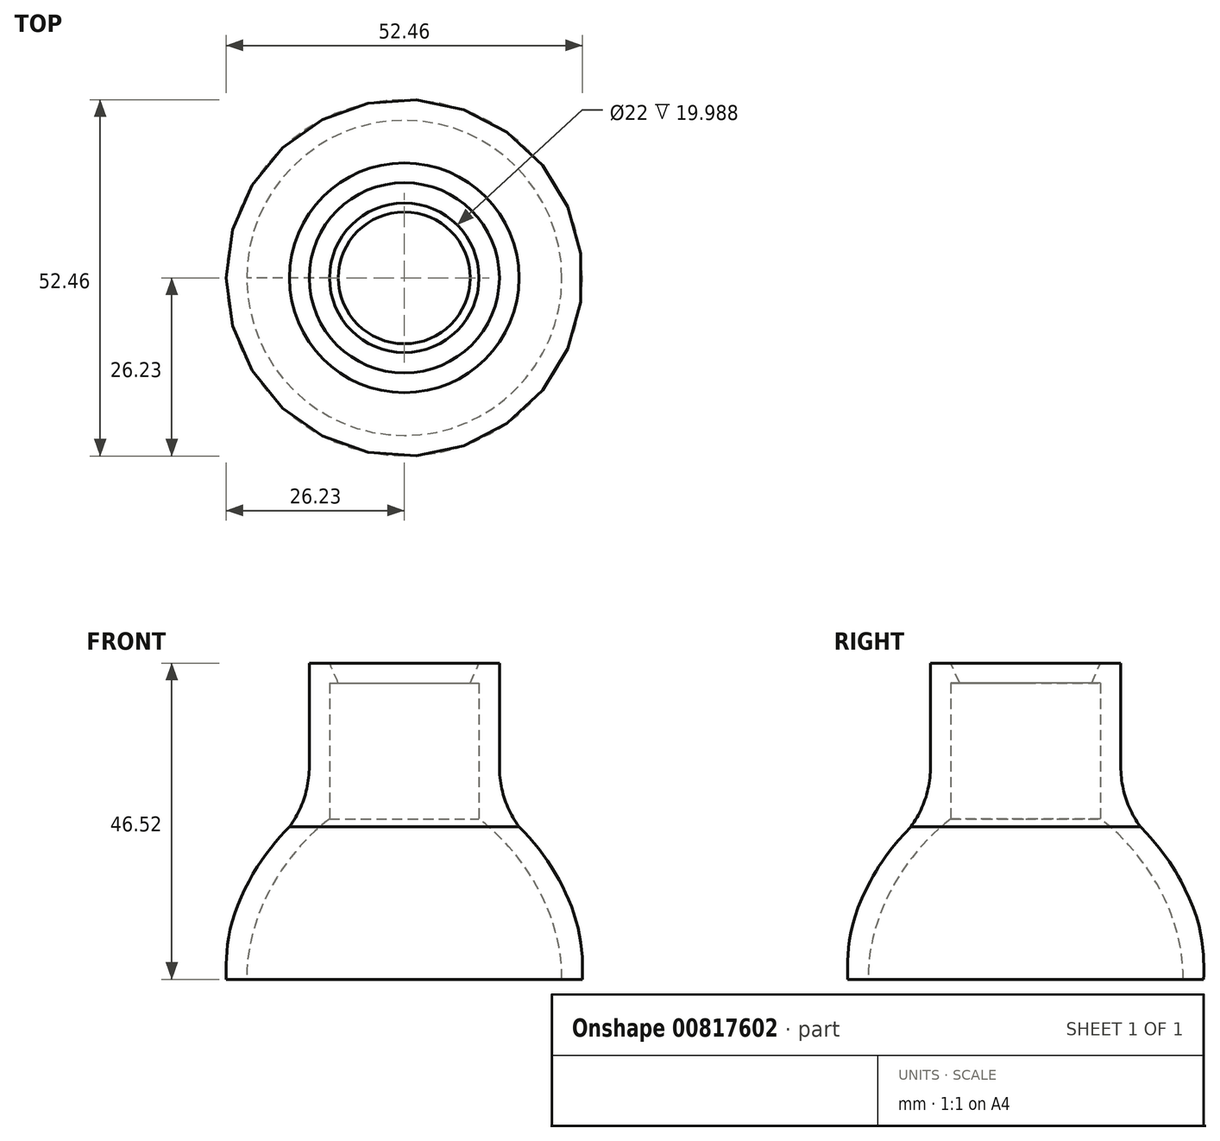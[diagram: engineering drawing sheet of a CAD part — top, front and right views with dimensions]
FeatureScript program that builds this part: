
annotation { "Feature Type Name" : "Feature", "Feature Type Description" : "" }
export const myFeature = defineFeature(function(context is Context, id is Id, definition is map)
    precondition{}
    {
        {
            var Q0;
            Q0=qCreatedBy(makeId("Front.planeOp"),FACE);
            var sketch = newSketch(context, id + "F0", { "sketchPlane" : qUnion([Q0])});
            skLineSegment(sketch, "E0", {"start": v(0, 10.51) * mm, "end": v(11, 10.51) * mm, "construction": true});
            skLineSegment(sketch, "E1", {"start": v(11, 10.51) * mm, "end": v(11, -4.97) * mm});
            skFitSpline(sketch, "E2", {"points": [v(11, -4.97) * mm, v(23.2, -28.57) * mm], "startDerivative": vector(15.73, -11.54) * mm, "endDerivative": vector(0, -33.05) * mm});
            skFitSpline(sketch, "E3.0", {"points": [v(12.77, -2.55) * mm, v(13.52, -3.1) * mm, v(15.04, -4.34) * mm, v(18.12, -7.41) * mm, v(21.82, -12.3) * mm, v(25.23, -19.68) * mm, v(26.2, -25.5) * mm, v(26.2, -28.57) * mm]});
            skLineSegment(sketch, "E4", {"start": v(23.2, -28.57) * mm, "end": v(26.2, -28.57) * mm});
            skLineSegment(sketch, "E5", {"start": v(26.2, -28.57) * mm, "end": v(26.2, -28.57) * mm});
            skLineSegment(sketch, "E6", {"start": v(14, 2.75) * mm, "end": v(14, 17.95) * mm});
            skPoint(sketch, "E7.visualSharp", {"position": v(14, -3.5) * mm});
            skArc(sketch, "E7.filletArc", {"start": v(14, 2.75) * mm, "mid": v(14.96, -2.54) * mm, "end": v(17.73, -7.15) * mm});
            skLineSegment(sketch, "E8", {"start": v(11, 10.51) * mm, "end": v(11, 17.95) * mm});
            skLineSegment(sketch, "E9", {"start": v(11, 17.95) * mm, "end": v(14, 17.95) * mm});
            skLineSegment(sketch, "E10", {"start": v(11, 17.95) * mm, "end": v(9.7, 15.02) * mm});
            skLineSegment(sketch, "E11", {"start": v(9.7, 15.02) * mm, "end": v(11, 15.02) * mm});
            skLineSegment(sketch, "E12", {"start": v(0, 0) * mm, "end": v(0, 29.18) * mm, "construction": true});
            skSolve(sketch);
        }
        {
            var Q0;
            {var subQ0=sQuery(id+"F0.wireOp",EDGE,"E10");Q0=makeQuery(id+"F0.imprint","IMPRINT",FACE,{"disambiguationData":[TD([[makeQuery(id+"F0.imprint","IMPRINT",EDGE,{"derivedFrom":subQ0}),1.0]])]});}
            var Q1;
            {var subQ0=sQuery(id+"F0.wireOp",EDGE,"E1");Q1=makeQuery(id+"F0.imprint","IMPRINT",FACE,{"disambiguationData":[TD([[makeQuery(id+"F0.imprint","IMPRINT",EDGE,{"derivedFrom":subQ0}),1.0]])]});}
            var Q2;
            Q2=sQuery(id+"F0.wireOp",EDGE,"E12");
            revolve(context, id + "F1", {"surfaceOperationType" : NewSurfaceOperationType.NEW, "entities" : qUnion([Q0, Q1]), "axis" : qUnion([Q2]), "revolveType" : RevolveType.FULL});
        }
    });
